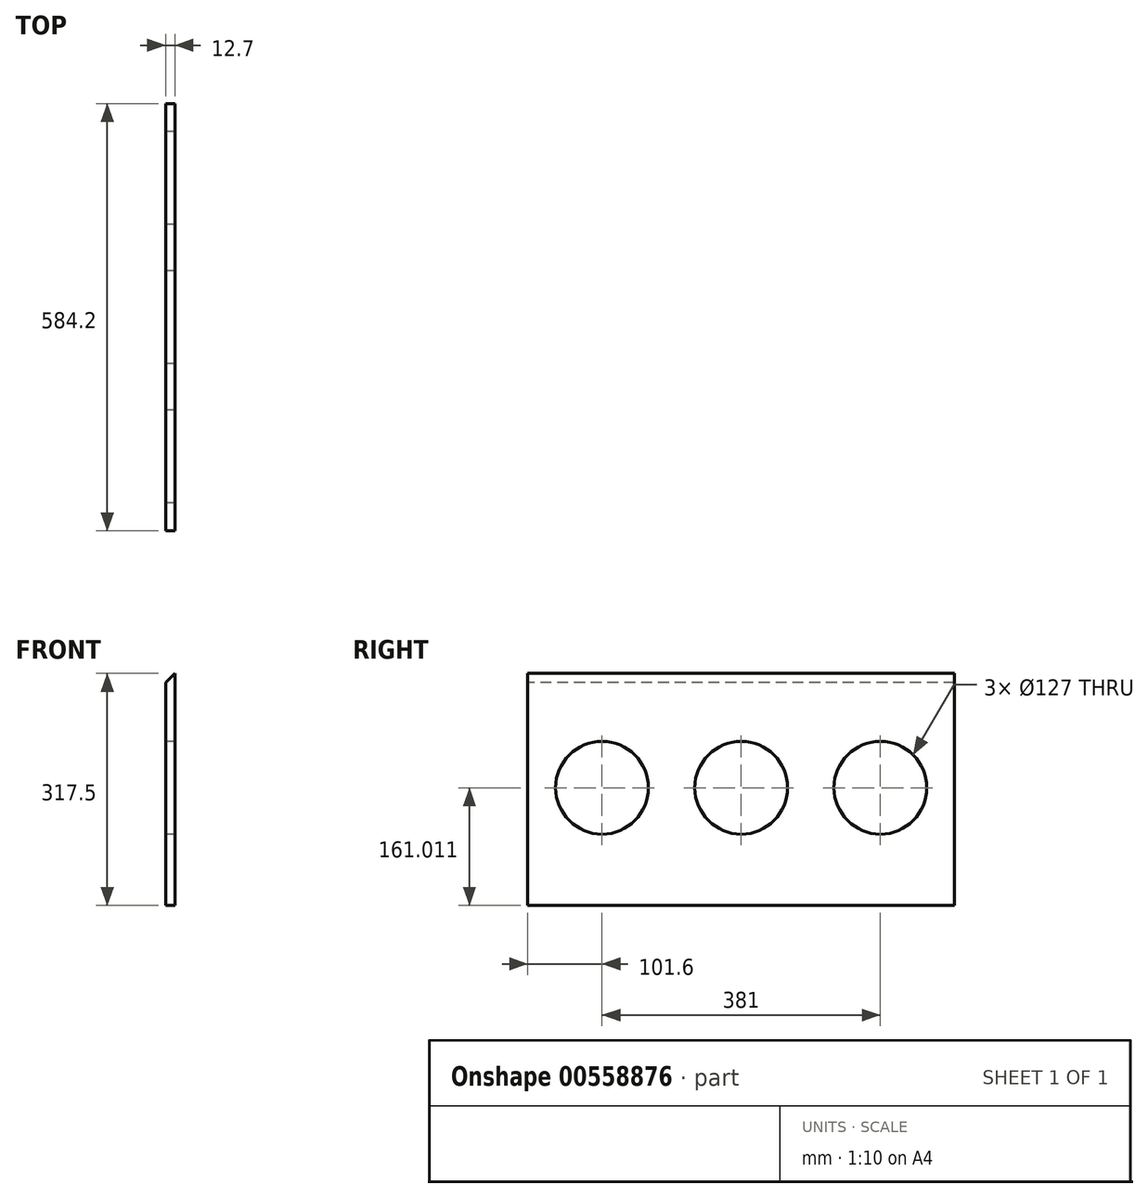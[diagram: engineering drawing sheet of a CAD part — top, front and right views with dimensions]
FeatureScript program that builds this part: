
annotation { "Feature Type Name" : "Feature", "Feature Type Description" : "" }
export const myFeature = defineFeature(function(context is Context, id is Id, definition is map)
    precondition{}
    {
        {
            var Q0;
            Q0=qCreatedBy(makeId("Front.planeOp"),FACE);
            var sketch = newSketch(context, id + "F0", { "sketchPlane" : qUnion([Q0])});
            skLineSegment(sketch, "E0", {"start": v(0, 0) * mm, "end": v(0, 304.8) * mm});
            skLineSegment(sketch, "E1", {"start": v(0, 304.8) * mm, "end": v(12.7, 317.5) * mm});
            skLineSegment(sketch, "E2", {"start": v(12.7, 317.5) * mm, "end": v(12.7, 0) * mm});
            skLineSegment(sketch, "E3", {"start": v(12.7, 0) * mm, "end": v(0, 0) * mm});
            skSolve(sketch);
        }
        {
            var Q0;
            Q0 = qSketchRegion(id + "F0", true);
            extrude(context, id + "F1", {"entities" : qUnion([Q0]), "oppositeDirection" : true, "depth" : 584.2 * mm, "offsetDistance" : 25.4 * mm});
        }
        {
            var Q0;
            Q0=qCreatedBy(makeId("Right.planeOp"),FACE);
            var sketch = newSketch(context, id + "F2", { "sketchPlane" : qUnion([Q0])});
            skLineSegment(sketch, "E4", {"start": v(-109.07, 161.01) * mm, "end": v(728.84, 161.01) * mm, "construction": true});
            skLineSegment(sketch, "E5", {"start": v(101.6, 276.2) * mm, "end": v(101.6, 32.7) * mm, "construction": true});
            skLineSegment(sketch, "E6", {"start": v(292.1, 269.63) * mm, "end": v(292.1, 32.7) * mm, "construction": true});
            skLineSegment(sketch, "E7", {"start": v(482.6, 272.61) * mm, "end": v(482.6, 32.7) * mm, "construction": true});
            skCircle(sketch, "E8", {"center": v(101.6, 161.01) * mm, "radius": 63.5 * mm});
            skCircle(sketch, "E9", {"center": v(292.1, 161.01) * mm, "radius": 63.5 * mm});
            skCircle(sketch, "E10", {"center": v(482.6, 161.01) * mm, "radius": 63.5 * mm});
            skSolve(sketch);
        }
        {
            var Q0;
            Q0 = qSketchRegion(id + "F2", true);
            extrude(context, id + "F3", {"entities" : qUnion([Q0]), "operationType" : NewBodyOperationType.REMOVE, "endBound" : BoundingType.THROUGH_ALL, "depth" : 25.4 * mm, "offsetDistance" : 25.4 * mm});
        }
    });
